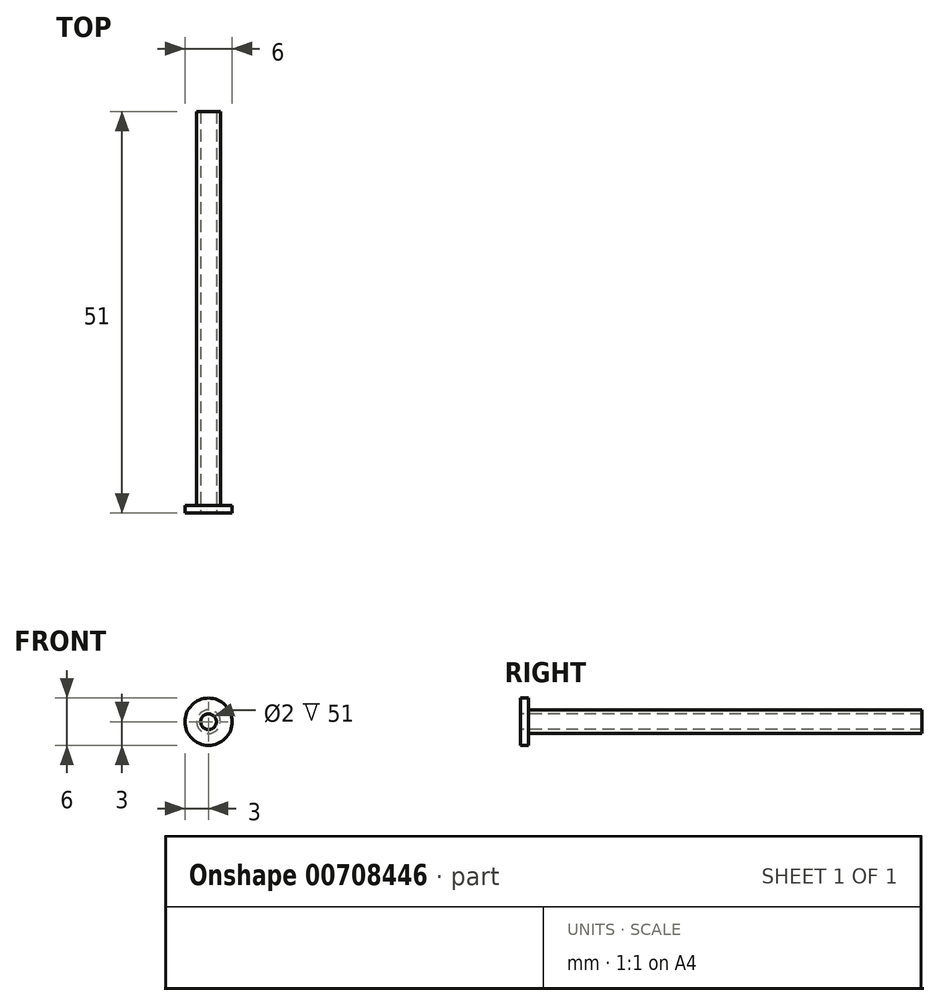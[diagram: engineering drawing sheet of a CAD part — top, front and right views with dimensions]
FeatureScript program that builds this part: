
annotation { "Feature Type Name" : "Feature", "Feature Type Description" : "" }
export const myFeature = defineFeature(function(context is Context, id is Id, definition is map)
    precondition{}
    {
        {
            var Q0;
            Q0=qCreatedBy(makeId("Front.planeOp"),FACE);
            var sketch = newSketch(context, id + "F0", { "sketchPlane" : qUnion([Q0])});
            skCircle(sketch, "E0", {"center": v(0, 0) * mm, "radius": 1.5 * mm});
            skSolve(sketch);
        }
        {
            var Q0;
            Q0=qSketchRegion(id+"F0",true);
            extrude(context, id + "F1", {"entities" : qUnion([Q0]), "depth" : 50 * mm, "offsetDistance" : 25 * mm});
        }
        {
            var Q0;
            Q0=makeQuery(id+"F1.opExtrude","CAP_FACE",FACE,{"disambiguationData":[OSD([sQuery(id+"F0.wireOp",EDGE,"E0")])],"isStart":false});
            var sketch = newSketch(context, id + "F2", { "sketchPlane" : qUnion([Q0])});
            skCircle(sketch, "E1", {"center": v(0, 0) * mm, "radius": 1 * mm});
            skSolve(sketch);
        }
        {
            var Q0;
            Q0=qSketchRegion(id+"F2",true);
            extrude(context, id + "F3", {"entities" : qUnion([Q0]), "operationType" : NewBodyOperationType.REMOVE, "endBound" : BoundingType.THROUGH_ALL, "oppositeDirection" : true, "depth" : 25 * mm, "offsetDistance" : 25 * mm});
        }
        {
            var Q0;
            Q0=makeQuery(id+"F1.opExtrude","CAP_FACE",FACE,{"disambiguationData":[OSD([sQuery(id+"F0.wireOp",EDGE,"E0")])],"isStart":false});
            var sketch = newSketch(context, id + "F4", { "sketchPlane" : qUnion([Q0])});
            skCircle(sketch, "E2", {"center": v(0, 0) * mm, "radius": 3 * mm});
            skSolve(sketch);
        }
        {
            var Q0;
            Q0=makeQuery(id+"F4.imprint","IMPRINT",FACE,{"disambiguationData":[TD([[makeQuery(id+"F4.imprint","IMPRINT",EDGE,{"derivedFrom":sQuery(id+"F4.wireOp",EDGE,"E2")}),1.0]])]});
            var sketch = newSketch(context, id + "F5", { "sketchPlane" : qUnion([Q0])});
            skCircle(sketch, "E3", {"center": v(0, 0) * mm, "radius": 1 * mm});
            skSolve(sketch);
        }
        {
            var Q0;
            Q0=makeQuery(id+"F4.imprint","IMPRINT",FACE,{"disambiguationData":[TD([[makeQuery(id+"F4.imprint","IMPRINT",EDGE,{"derivedFrom":makeQuery(id+"F1.opExtrude","CAP_EDGE",EDGE,{"disambiguationData":[OSD([sQuery(id+"F0.wireOp",EDGE,"E0")])],"isStart":false})}),1.0]])]});
            var Q1;
            Q1=makeQuery(id+"F5.imprint","IMPRINT",FACE,{"disambiguationData":[TD([[makeQuery(id+"F5.imprint","IMPRINT",EDGE,{"derivedFrom":makeQuery(id+"F4.imprint","IMPRINT",EDGE,{"derivedFrom":sQuery(id+"F4.wireOp",EDGE,"E2")})}),1.0]])]});
            extrude(context, id + "F6", {"entities" : qUnion([Q0, Q1]), "operationType" : NewBodyOperationType.ADD, "depth" : 1 * mm, "offsetDistance" : 25 * mm});
        }
    });
